# Revit family: RN 90024 Optifitt-Serra-Réduction
name_source: partatom
category: Rohrformteile
units: mm (PartAtom-declared; Revit-internal decimal feet)

## family parameters
Arbeitsebenenbasiert = Nein
Beim Laden mit Abzugskörper schneiden = Nein
Bemaßung runder Anschluss = Durchmesser verwenden
Gemeinsam genutzt = Nein
Immer vertikal = Ja
Teiletyp = Übergang

## types (26) — shared parameters
1.010.00.2 Blattnummer der Richtlinie = 29
1.010.00.3 Ausgabedatum (Monat) der Richtlinie = 201308
1.010.00.4 Herstellername = R. Nussbaum AG
1.010.00.5 Revisionsdatum der Datei = 20190521
1.010.00.6 Webadresse des Herstellers = http://www.nussbaum.ch
1.100.00.4 Produktbezeichnung = Versorgung
1.110.00.2 Index = 3
1.110.00.4 Produktbezeichnung = Optifitt-Serra
1.960/3L.00.8 Link (URL) = https://www.nussbaum.ch
29.700.00.4 Produktname = Optifitt-Serra-Reduktion
29.700.00.5 Produktkennung = 2
29.700.00.6 Querschnittsform = 1
29.700.00.7 Nennweitensystem = DN
29.700.00.8 Nenndrucksystem = PN
29.710.02.4 Nenndruck = 16
29.710.02.5 max. zul. Überdruck [hPa] = 1600
29.710.02.7 max. zul. Dauer-Betriebsdruck [hPa] = 1600
29.710.02.9 max. zul. Dauer-Betriebstemperatur [°C] = 90
Connector Visibility = Nein
EnclosingSpace Visibility = Nein
R. Nussbaum AG 90024.47 de Visibility = Nein

## per-type parameters (varying)
- DN=50x32: 1.800.00.3 TGA-Nummer=01900300000000000000000000000000000000000000000014000000000000000045; 1.800.00.4 Kommentarfeld=90024.40, Optifitt-Serra-Reduktion, DN=50x32, L=37, R=2, Rp=1¼; 1.810.00.3 Hersteller-Bestellnummer=90024.40; 1.810.00.4 DATANORM-Nummer=90024.40; 1.810.00.6 GTIN-Nummer=7612945033598; 29.710.02.10 Formstück-Gewicht [kg]=0.342; 29.710.02.3 Benennung=Optifitt-Serra-Reduktion, DN=50x32, L=37, R=2, Rp=1¼; CONNECTOR0_DIAMETER_dX_0r=32 mm; CONNECTOR0_dX_01=19 mm; CONNECTOR0_ref_dX=19 mm; CONNECTOR1_DIAMETER_dX_0r=50 mm; CONNECTOR1_dX_00=13 mm; CONNECTOR1_dX_01=37 mm; CONNECTOR1_ref_dX=37 mm; R. Nussbaum AG 90024.20 de Visibility=Nein; R. Nussbaum AG 90024.21 de Visibility=Nein; R. Nussbaum AG 90024.22 de Visibility=Nein; R. Nussbaum AG 90024.23 de Visibility=Nein; R. Nussbaum AG 90024.25 de Visibility=Nein; R. Nussbaum AG 90024.26 de Visibility=Nein; R. Nussbaum AG 90024.27 de Visibility=Nein; R. Nussbaum AG 90024.28 de Visibility=Nein; R. Nussbaum AG 90024.29 de Visibility=Nein; R. Nussbaum AG 90024.30 de Visibility=Nein; R. Nussbaum AG 90024.31 de Visibility=Nein; R. Nussbaum AG 90024.32 de Visibility=Nein; R. Nussbaum AG 90024.33 de Visibility=Nein; R. Nussbaum AG 90024.34 de Visibility=Nein; R. Nussbaum AG 90024.35 de Visibility=Nein; R. Nussbaum AG 90024.36 de Visibility=Nein; R. Nussbaum AG 90024.37 de Visibility=Nein; R. Nussbaum AG 90024.38 de Visibility=Nein; R. Nussbaum AG 90024.39 de Visibility=Nein; R. Nussbaum AG 90024.40 de Visibility=Ja; R. Nussbaum AG 90024.41 de Visibility=Nein; R. Nussbaum AG 90024.42 de Visibility=Nein; R. Nussbaum AG 90024.43 de Visibility=Nein; R. Nussbaum AG 90024.44 de Visibility=Nein; R. Nussbaum AG 90024.45 de Visibility=Nein; R. Nussbaum AG 90024.46 de Visibility=Nein
- DN=32x15: 1.800.00.3 TGA-Nummer=01900300000000000000000000000000000000000000000014000000000000000044; 1.800.00.4 Kommentarfeld=90024.30, Optifitt-Serra-Reduktion, DN=32x15, L=31, R=1¼, Rp=½; 1.810.00.3 Hersteller-Bestellnummer=90024.30; 1.810.00.4 DATANORM-Nummer=90024.30; 1.810.00.6 GTIN-Nummer=7612945033499; 29.710.02.10 Formstück-Gewicht [kg]=0.168; 29.710.02.3 Benennung=Optifitt-Serra-Reduktion, DN=32x15, L=31, R=1¼, Rp=½; CONNECTOR0_DIAMETER_dX_0r=15 mm; CONNECTOR0_dX_01=13 mm; CONNECTOR0_ref_dX=13 mm; CONNECTOR1_DIAMETER_dX_0r=32 mm; CONNECTOR1_dX_00=12 mm  [stored 0.0393701 ft]; CONNECTOR1_dX_01=31 mm; CONNECTOR1_ref_dX=31 mm; R. Nussbaum AG 90024.20 de Visibility=Nein; R. Nussbaum AG 90024.21 de Visibility=Nein; R. Nussbaum AG 90024.22 de Visibility=Nein; R. Nussbaum AG 90024.23 de Visibility=Nein; R. Nussbaum AG 90024.25 de Visibility=Nein; R. Nussbaum AG 90024.26 de Visibility=Nein; R. Nussbaum AG 90024.27 de Visibility=Nein; R. Nussbaum AG 90024.28 de Visibility=Nein; R. Nussbaum AG 90024.29 de Visibility=Nein; R. Nussbaum AG 90024.30 de Visibility=Ja; R. Nussbaum AG 90024.31 de Visibility=Nein; R. Nussbaum AG 90024.32 de Visibility=Nein; R. Nussbaum AG 90024.33 de Visibility=Nein; R. Nussbaum AG 90024.34 de Visibility=Nein; R. Nussbaum AG 90024.35 de Visibility=Nein; R. Nussbaum AG 90024.36 de Visibility=Nein; R. Nussbaum AG 90024.37 de Visibility=Nein; R. Nussbaum AG 90024.38 de Visibility=Nein; R. Nussbaum AG 90024.39 de Visibility=Nein; R. Nussbaum AG 90024.40 de Visibility=Nein; R. Nussbaum AG 90024.41 de Visibility=Nein; R. Nussbaum AG 90024.42 de Visibility=Nein; R. Nussbaum AG 90024.43 de Visibility=Nein; R. Nussbaum AG 90024.44 de Visibility=Nein; R. Nussbaum AG 90024.45 de Visibility=Nein; R. Nussbaum AG 90024.46 de Visibility=Nein
- DN=12x6: 1.800.00.3 TGA-Nummer=01900300000000000000000000000000000000000000000014000000000000000043; 1.800.00.4 Kommentarfeld=90024.20, Optifitt-Serra-Reduktion, DN=12x6, L=17, R=3/8, Rp=1/8; 1.810.00.3 Hersteller-Bestellnummer=90024.20; 1.810.00.4 DATANORM-Nummer=90024.20; 1.810.00.6 GTIN-Nummer=7612945723642; 29.710.02.10 Formstück-Gewicht [kg]=0.016; 29.710.02.3 Benennung=Optifitt-Serra-Reduktion, DN=12x6, L=17, R=3/8, Rp=1/8; CONNECTOR0_DIAMETER_dX_0r=6 mm  [stored 0.019685 ft]; CONNECTOR0_dX_01=7 mm  [stored 0.0229659 ft]; CONNECTOR0_ref_dX=7 mm  [stored 0.0229659 ft]; CONNECTOR1_DIAMETER_dX_0r=10 mm  [stored 0.0328084 ft]; CONNECTOR1_dX_00=7 mm  [stored 0.0229659 ft]; CONNECTOR1_dX_01=17 mm; CONNECTOR1_ref_dX=17 mm; R. Nussbaum AG 90024.20 de Visibility=Ja; R. Nussbaum AG 90024.21 de Visibility=Nein; R. Nussbaum AG 90024.22 de Visibility=Nein; R. Nussbaum AG 90024.23 de Visibility=Nein; R. Nussbaum AG 90024.25 de Visibility=Nein; R. Nussbaum AG 90024.26 de Visibility=Nein; R. Nussbaum AG 90024.27 de Visibility=Nein; R. Nussbaum AG 90024.28 de Visibility=Nein; R. Nussbaum AG 90024.29 de Visibility=Nein; R. Nussbaum AG 90024.30 de Visibility=Nein; R. Nussbaum AG 90024.31 de Visibility=Nein; R. Nussbaum AG 90024.32 de Visibility=Nein; R. Nussbaum AG 90024.33 de Visibility=Nein; R. Nussbaum AG 90024.34 de Visibility=Nein; R. Nussbaum AG 90024.35 de Visibility=Nein; R. Nussbaum AG 90024.36 de Visibility=Nein; R. Nussbaum AG 90024.37 de Visibility=Nein; R. Nussbaum AG 90024.38 de Visibility=Nein; R. Nussbaum AG 90024.39 de Visibility=Nein; R. Nussbaum AG 90024.40 de Visibility=Nein; R. Nussbaum AG 90024.41 de Visibility=Nein; R. Nussbaum AG 90024.42 de Visibility=Nein; R. Nussbaum AG 90024.43 de Visibility=Nein; R. Nussbaum AG 90024.44 de Visibility=Nein; R. Nussbaum AG 90024.45 de Visibility=Nein; R. Nussbaum AG 90024.46 de Visibility=Nein
- DN=80x65: 1.800.00.3 TGA-Nummer=01900300000000000000000000000000000000000000000014000000000000000023; 1.800.00.4 Kommentarfeld=90024.46, Optifitt-Serra-Reduktion, DN=80x65, L=47, R=3, Rp=2½; 1.810.00.3 Hersteller-Bestellnummer=90024.46; 1.810.00.4 DATANORM-Nummer=90024.46; 1.810.00.6 GTIN-Nummer=7612945723659; 29.710.02.10 Formstück-Gewicht [kg]=0.614; 29.710.02.3 Benennung=Optifitt-Serra-Reduktion, DN=80x65, L=47, R=3, Rp=2½; CONNECTOR0_DIAMETER_dX_0r=65 mm; CONNECTOR0_dX_01=27 mm; CONNECTOR0_ref_dX=27 mm; CONNECTOR1_DIAMETER_dX_0r=80 mm; CONNECTOR1_dX_00=17 mm; CONNECTOR1_dX_01=47 mm; CONNECTOR1_ref_dX=47 mm; Hersteller=R. Nussbaum AG; Modell=90024.46; R. Nussbaum AG 90024.20 de Visibility=Nein; R. Nussbaum AG 90024.21 de Visibility=Nein; R. Nussbaum AG 90024.22 de Visibility=Nein; R. Nussbaum AG 90024.23 de Visibility=Nein; R. Nussbaum AG 90024.25 de Visibility=Nein; R. Nussbaum AG 90024.26 de Visibility=Nein; R. Nussbaum AG 90024.27 de Visibility=Nein; R. Nussbaum AG 90024.28 de Visibility=Nein; R. Nussbaum AG 90024.29 de Visibility=Nein; R. Nussbaum AG 90024.30 de Visibility=Nein; R. Nussbaum AG 90024.31 de Visibility=Nein; R. Nussbaum AG 90024.32 de Visibility=Nein; R. Nussbaum AG 90024.33 de Visibility=Nein; R. Nussbaum AG 90024.34 de Visibility=Nein; R. Nussbaum AG 90024.35 de Visibility=Nein; R. Nussbaum AG 90024.36 de Visibility=Nein; R. Nussbaum AG 90024.37 de Visibility=Nein; R. Nussbaum AG 90024.38 de Visibility=Nein; R. Nussbaum AG 90024.39 de Visibility=Nein; R. Nussbaum AG 90024.40 de Visibility=Nein; R. Nussbaum AG 90024.41 de Visibility=Nein; R. Nussbaum AG 90024.42 de Visibility=Nein; R. Nussbaum AG 90024.43 de Visibility=Nein; R. Nussbaum AG 90024.44 de Visibility=Nein; R. Nussbaum AG 90024.45 de Visibility=Nein; R. Nussbaum AG 90024.46 de Visibility=Ja; Typenkommentare=Optifitt-Serra-Réduction DN=80x65; URL=https://www.nussbaum.ch
- DN=65x50: 1.800.00.3 TGA-Nummer=01900300000000000000000000000000000000000000000014000000000000000022; 1.800.00.4 Kommentarfeld=90024.45, Optifitt-Serra-Reduktion, DN=65x50, L=41, R=2½, Rp=2; 1.810.00.3 Hersteller-Bestellnummer=90024.45; 1.810.00.4 DATANORM-Nummer=90024.45; 1.810.00.5 StLB-Nummer=214.538; 1.810.00.6 GTIN-Nummer=7612945033642; 29.710.02.10 Formstück-Gewicht [kg]=0.495; 29.710.02.3 Benennung=Optifitt-Serra-Reduktion, DN=65x50, L=41, R=2½, Rp=2; CONNECTOR0_DIAMETER_dX_0r=50 mm; CONNECTOR0_dX_01=24 mm; CONNECTOR0_ref_dX=24 mm; CONNECTOR1_DIAMETER_dX_0r=65 mm; CONNECTOR1_dX_00=14 mm  [stored 0.0459318 ft]; CONNECTOR1_dX_01=41 mm; CONNECTOR1_ref_dX=41 mm; Hersteller=R. Nussbaum AG; Modell=90024.45; R. Nussbaum AG 90024.20 de Visibility=Nein; R. Nussbaum AG 90024.21 de Visibility=Nein; R. Nussbaum AG 90024.22 de Visibility=Nein; R. Nussbaum AG 90024.23 de Visibility=Nein; R. Nussbaum AG 90024.25 de Visibility=Nein; R. Nussbaum AG 90024.26 de Visibility=Nein; R. Nussbaum AG 90024.27 de Visibility=Nein; R. Nussbaum AG 90024.28 de Visibility=Nein; R. Nussbaum AG 90024.29 de Visibility=Nein; R. Nussbaum AG 90024.30 de Visibility=Nein; R. Nussbaum AG 90024.31 de Visibility=Nein; R. Nussbaum AG 90024.32 de Visibility=Nein; R. Nussbaum AG 90024.33 de Visibility=Nein; R. Nussbaum AG 90024.34 de Visibility=Nein; R. Nussbaum AG 90024.35 de Visibility=Nein; R. Nussbaum AG 90024.36 de Visibility=Nein; R. Nussbaum AG 90024.37 de Visibility=Nein; R. Nussbaum AG 90024.38 de Visibility=Nein; R. Nussbaum AG 90024.39 de Visibility=Nein; R. Nussbaum AG 90024.40 de Visibility=Nein; R. Nussbaum AG 90024.41 de Visibility=Nein; R. Nussbaum AG 90024.42 de Visibility=Nein; R. Nussbaum AG 90024.43 de Visibility=Nein; R. Nussbaum AG 90024.44 de Visibility=Nein; R. Nussbaum AG 90024.45 de Visibility=Ja; R. Nussbaum AG 90024.46 de Visibility=Nein; Typenkommentare=Optifitt-Serra-Réduction DN=65x50; URL=https://www.nussbaum.ch
- DN=65x40: 1.800.00.3 TGA-Nummer=01900300000000000000000000000000000000000000000014000000000000000021; 1.800.00.4 Kommentarfeld=90024.44, Optifitt-Serra-Reduktion, DN=65x40, L=41, R=2½, Rp=1½; 1.810.00.3 Hersteller-Bestellnummer=90024.44; 1.810.00.4 DATANORM-Nummer=90024.44; 1.810.00.6 GTIN-Nummer=7612945033635; 29.710.02.10 Formstück-Gewicht [kg]=0.609; 29.710.02.3 Benennung=Optifitt-Serra-Reduktion, DN=65x40, L=41, R=2½, Rp=1½; CONNECTOR0_DIAMETER_dX_0r=40 mm; CONNECTOR0_dX_01=19 mm; CONNECTOR0_ref_dX=19 mm; CONNECTOR1_DIAMETER_dX_0r=65 mm; CONNECTOR1_dX_00=14 mm  [stored 0.0459318 ft]; CONNECTOR1_dX_01=41 mm; CONNECTOR1_ref_dX=41 mm; Hersteller=R. Nussbaum AG; Modell=90024.44; R. Nussbaum AG 90024.20 de Visibility=Nein; R. Nussbaum AG 90024.21 de Visibility=Nein; R. Nussbaum AG 90024.22 de Visibility=Nein; R. Nussbaum AG 90024.23 de Visibility=Nein; R. Nussbaum AG 90024.25 de Visibility=Nein; R. Nussbaum AG 90024.26 de Visibility=Nein; R. Nussbaum AG 90024.27 de Visibility=Nein; R. Nussbaum AG 90024.28 de Visibility=Nein; R. Nussbaum AG 90024.29 de Visibility=Nein; R. Nussbaum AG 90024.30 de Visibility=Nein; R. Nussbaum AG 90024.31 de Visibility=Nein; R. Nussbaum AG 90024.32 de Visibility=Nein; R. Nussbaum AG 90024.33 de Visibility=Nein; R. Nussbaum AG 90024.34 de Visibility=Nein; R. Nussbaum AG 90024.35 de Visibility=Nein; R. Nussbaum AG 90024.36 de Visibility=Nein; R. Nussbaum AG 90024.37 de Visibility=Nein; R. Nussbaum AG 90024.38 de Visibility=Nein; R. Nussbaum AG 90024.39 de Visibility=Nein; R. Nussbaum AG 90024.40 de Visibility=Nein; R. Nussbaum AG 90024.41 de Visibility=Nein; R. Nussbaum AG 90024.42 de Visibility=Nein; R. Nussbaum AG 90024.43 de Visibility=Nein; R. Nussbaum AG 90024.44 de Visibility=Ja; R. Nussbaum AG 90024.45 de Visibility=Nein; R. Nussbaum AG 90024.46 de Visibility=Nein; Typenkommentare=Optifitt-Serra-Réduction DN=65x40; URL=https://www.nussbaum.ch
- DN=65x32: 1.800.00.3 TGA-Nummer=01900300000000000000000000000000000000000000000014000000000000000020; 1.800.00.4 Kommentarfeld=90024.43, Optifitt-Serra-Reduktion, DN=65x32, L=41, R=2½, Rp=1¼; 1.810.00.3 Hersteller-Bestellnummer=90024.43; 1.810.00.4 DATANORM-Nummer=90024.43; 1.810.00.6 GTIN-Nummer=7612945033628; 29.710.02.10 Formstück-Gewicht [kg]=0.662; 29.710.02.3 Benennung=Optifitt-Serra-Reduktion, DN=65x32, L=41, R=2½, Rp=1¼; CONNECTOR0_DIAMETER_dX_0r=32 mm; CONNECTOR0_dX_01=19 mm; CONNECTOR0_ref_dX=19 mm; CONNECTOR1_DIAMETER_dX_0r=65 mm; CONNECTOR1_dX_00=14 mm  [stored 0.0459318 ft]; CONNECTOR1_dX_01=41 mm; CONNECTOR1_ref_dX=41 mm; Hersteller=R. Nussbaum AG; Modell=90024.43; R. Nussbaum AG 90024.20 de Visibility=Nein; R. Nussbaum AG 90024.21 de Visibility=Nein; R. Nussbaum AG 90024.22 de Visibility=Nein; R. Nussbaum AG 90024.23 de Visibility=Nein; R. Nussbaum AG 90024.25 de Visibility=Nein; R. Nussbaum AG 90024.26 de Visibility=Nein; R. Nussbaum AG 90024.27 de Visibility=Nein; R. Nussbaum AG 90024.28 de Visibility=Nein; R. Nussbaum AG 90024.29 de Visibility=Nein; R. Nussbaum AG 90024.30 de Visibility=Nein; R. Nussbaum AG 90024.31 de Visibility=Nein; R. Nussbaum AG 90024.32 de Visibility=Nein; R. Nussbaum AG 90024.33 de Visibility=Nein; R. Nussbaum AG 90024.34 de Visibility=Nein; R. Nussbaum AG 90024.35 de Visibility=Nein; R. Nussbaum AG 90024.36 de Visibility=Nein; R. Nussbaum AG 90024.37 de Visibility=Nein; R. Nussbaum AG 90024.38 de Visibility=Nein; R. Nussbaum AG 90024.39 de Visibility=Nein; R. Nussbaum AG 90024.40 de Visibility=Nein; R. Nussbaum AG 90024.41 de Visibility=Nein; R. Nussbaum AG 90024.42 de Visibility=Nein; R. Nussbaum AG 90024.43 de Visibility=Ja; R. Nussbaum AG 90024.44 de Visibility=Nein; R. Nussbaum AG 90024.45 de Visibility=Nein; R. Nussbaum AG 90024.46 de Visibility=Nein; Typenkommentare=Optifitt-Serra-Réduction DN=65x32; URL=https://www.nussbaum.ch
- DN=65x25: 1.800.00.3 TGA-Nummer=01900300000000000000000000000000000000000000000014000000000000000019; 1.800.00.4 Kommentarfeld=90024.42, Optifitt-Serra-Reduktion, DN=65x25, L=41, R=2½, Rp=1; 1.810.00.3 Hersteller-Bestellnummer=90024.42; 1.810.00.4 DATANORM-Nummer=90024.42; 1.810.00.6 GTIN-Nummer=7612945033611; 29.710.02.10 Formstück-Gewicht [kg]=0.679; 29.710.02.3 Benennung=Optifitt-Serra-Reduktion, DN=65x25, L=41, R=2½, Rp=1; CONNECTOR0_DIAMETER_dX_0r=25 mm  [stored 0.082021 ft]; CONNECTOR0_dX_01=17 mm; CONNECTOR0_ref_dX=17 mm; CONNECTOR1_DIAMETER_dX_0r=65 mm; CONNECTOR1_dX_00=14 mm  [stored 0.0459318 ft]; CONNECTOR1_dX_01=41 mm; CONNECTOR1_ref_dX=41 mm; Hersteller=R. Nussbaum AG; Modell=90024.42; R. Nussbaum AG 90024.20 de Visibility=Nein; R. Nussbaum AG 90024.21 de Visibility=Nein; R. Nussbaum AG 90024.22 de Visibility=Nein; R. Nussbaum AG 90024.23 de Visibility=Nein; R. Nussbaum AG 90024.25 de Visibility=Nein; R. Nussbaum AG 90024.26 de Visibility=Nein; R. Nussbaum AG 90024.27 de Visibility=Nein; R. Nussbaum AG 90024.28 de Visibility=Nein; R. Nussbaum AG 90024.29 de Visibility=Nein; R. Nussbaum AG 90024.30 de Visibility=Nein; R. Nussbaum AG 90024.31 de Visibility=Nein; R. Nussbaum AG 90024.32 de Visibility=Nein; R. Nussbaum AG 90024.33 de Visibility=Nein; R. Nussbaum AG 90024.34 de Visibility=Nein; R. Nussbaum AG 90024.35 de Visibility=Nein; R. Nussbaum AG 90024.36 de Visibility=Nein; R. Nussbaum AG 90024.37 de Visibility=Nein; R. Nussbaum AG 90024.38 de Visibility=Nein; R. Nussbaum AG 90024.39 de Visibility=Nein; R. Nussbaum AG 90024.40 de Visibility=Nein; R. Nussbaum AG 90024.41 de Visibility=Nein; R. Nussbaum AG 90024.42 de Visibility=Ja; R. Nussbaum AG 90024.43 de Visibility=Nein; R. Nussbaum AG 90024.44 de Visibility=Nein; R. Nussbaum AG 90024.45 de Visibility=Nein; R. Nussbaum AG 90024.46 de Visibility=Nein; Typenkommentare=Optifitt-Serra-Réduction DN=65x25; URL=https://www.nussbaum.ch
- DN=50x40: 1.800.00.3 TGA-Nummer=01900300000000000000000000000000000000000000000014000000000000000018; 1.800.00.4 Kommentarfeld=90024.41, Optifitt-Serra-Reduktion, DN=50x40, L=37, R=2, Rp=1½; 1.810.00.3 Hersteller-Bestellnummer=90024.41; 1.810.00.4 DATANORM-Nummer=90024.41; 1.810.00.5 StLB-Nummer=214.537; 1.810.00.6 GTIN-Nummer=7612945033604; 29.710.02.10 Formstück-Gewicht [kg]=0.287; 29.710.02.3 Benennung=Optifitt-Serra-Reduktion, DN=50x40, L=37, R=2, Rp=1½; CONNECTOR0_DIAMETER_dX_0r=40 mm; CONNECTOR0_dX_01=19 mm; CONNECTOR0_ref_dX=19 mm; CONNECTOR1_DIAMETER_dX_0r=50 mm; CONNECTOR1_dX_00=13 mm; CONNECTOR1_dX_01=37 mm; CONNECTOR1_ref_dX=37 mm; Hersteller=R. Nussbaum AG; Modell=90024.41; R. Nussbaum AG 90024.20 de Visibility=Nein; R. Nussbaum AG 90024.21 de Visibility=Nein; R. Nussbaum AG 90024.22 de Visibility=Nein; R. Nussbaum AG 90024.23 de Visibility=Nein; R. Nussbaum AG 90024.25 de Visibility=Nein; R. Nussbaum AG 90024.26 de Visibility=Nein; R. Nussbaum AG 90024.27 de Visibility=Nein; R. Nussbaum AG 90024.28 de Visibility=Nein; R. Nussbaum AG 90024.29 de Visibility=Nein; R. Nussbaum AG 90024.30 de Visibility=Nein; R. Nussbaum AG 90024.31 de Visibility=Nein; R. Nussbaum AG 90024.32 de Visibility=Nein; R. Nussbaum AG 90024.33 de Visibility=Nein; R. Nussbaum AG 90024.34 de Visibility=Nein; R. Nussbaum AG 90024.35 de Visibility=Nein; R. Nussbaum AG 90024.36 de Visibility=Nein; R. Nussbaum AG 90024.37 de Visibility=Nein; R. Nussbaum AG 90024.38 de Visibility=Nein; R. Nussbaum AG 90024.39 de Visibility=Nein; R. Nussbaum AG 90024.40 de Visibility=Nein; R. Nussbaum AG 90024.41 de Visibility=Ja; R. Nussbaum AG 90024.42 de Visibility=Nein; R. Nussbaum AG 90024.43 de Visibility=Nein; R. Nussbaum AG 90024.44 de Visibility=Nein; R. Nussbaum AG 90024.45 de Visibility=Nein; R. Nussbaum AG 90024.46 de Visibility=Nein; Typenkommentare=Optifitt-Serra-Réduction DN=50x40; URL=https://www.nussbaum.ch
- DN=50x25: 1.800.00.3 TGA-Nummer=01900300000000000000000000000000000000000000000014000000000000000017; 1.800.00.4 Kommentarfeld=90024.39, Optifitt-Serra-Reduktion, DN=50x25, L=37, R=2, Rp=1; 1.810.00.3 Hersteller-Bestellnummer=90024.39; 1.810.00.4 DATANORM-Nummer=90024.39; 1.810.00.6 GTIN-Nummer=7612945033581; 29.710.02.10 Formstück-Gewicht [kg]=0.395; 29.710.02.3 Benennung=Optifitt-Serra-Reduktion, DN=50x25, L=37, R=2, Rp=1; CONNECTOR0_DIAMETER_dX_0r=25 mm  [stored 0.082021 ft]; CONNECTOR0_dX_01=17 mm; CONNECTOR0_ref_dX=17 mm; CONNECTOR1_DIAMETER_dX_0r=50 mm; CONNECTOR1_dX_00=13 mm; CONNECTOR1_dX_01=37 mm; CONNECTOR1_ref_dX=37 mm; Hersteller=R. Nussbaum AG; Modell=90024.39; R. Nussbaum AG 90024.20 de Visibility=Nein; R. Nussbaum AG 90024.21 de Visibility=Nein; R. Nussbaum AG 90024.22 de Visibility=Nein; R. Nussbaum AG 90024.23 de Visibility=Nein; R. Nussbaum AG 90024.25 de Visibility=Nein; R. Nussbaum AG 90024.26 de Visibility=Nein; R. Nussbaum AG 90024.27 de Visibility=Nein; R. Nussbaum AG 90024.28 de Visibility=Nein; R. Nussbaum AG 90024.29 de Visibility=Nein; R. Nussbaum AG 90024.30 de Visibility=Nein; R. Nussbaum AG 90024.31 de Visibility=Nein; R. Nussbaum AG 90024.32 de Visibility=Nein; R. Nussbaum AG 90024.33 de Visibility=Nein; R. Nussbaum AG 90024.34 de Visibility=Nein; R. Nussbaum AG 90024.35 de Visibility=Nein; R. Nussbaum AG 90024.36 de Visibility=Nein; R. Nussbaum AG 90024.37 de Visibility=Nein; R. Nussbaum AG 90024.38 de Visibility=Nein; R. Nussbaum AG 90024.39 de Visibility=Ja; R. Nussbaum AG 90024.40 de Visibility=Nein; R. Nussbaum AG 90024.41 de Visibility=Nein; R. Nussbaum AG 90024.42 de Visibility=Nein; R. Nussbaum AG 90024.43 de Visibility=Nein; R. Nussbaum AG 90024.44 de Visibility=Nein; R. Nussbaum AG 90024.45 de Visibility=Nein; R. Nussbaum AG 90024.46 de Visibility=Nein; Typenkommentare=Optifitt-Serra-Réduction DN=50x25; URL=https://www.nussbaum.ch
- DN=50x20: 1.800.00.3 TGA-Nummer=01900300000000000000000000000000000000000000000014000000000000000016; 1.800.00.4 Kommentarfeld=90024.38, Optifitt-Serra-Reduktion, DN=50x20, L=37, R=2, Rp=¾; 1.810.00.3 Hersteller-Bestellnummer=90024.38; 1.810.00.4 DATANORM-Nummer=90024.38; 1.810.00.6 GTIN-Nummer=7612945033574; 29.710.02.10 Formstück-Gewicht [kg]=0.396; 29.710.02.3 Benennung=Optifitt-Serra-Reduktion, DN=50x20, L=37, R=2, Rp=¾; CONNECTOR0_DIAMETER_dX_0r=20 mm; CONNECTOR0_dX_01=15 mm; CONNECTOR0_ref_dX=15 mm; CONNECTOR1_DIAMETER_dX_0r=50 mm; CONNECTOR1_dX_00=13 mm; CONNECTOR1_dX_01=37 mm; CONNECTOR1_ref_dX=37 mm; Hersteller=R. Nussbaum AG; Modell=90024.38; R. Nussbaum AG 90024.20 de Visibility=Nein; R. Nussbaum AG 90024.21 de Visibility=Nein; R. Nussbaum AG 90024.22 de Visibility=Nein; R. Nussbaum AG 90024.23 de Visibility=Nein; R. Nussbaum AG 90024.25 de Visibility=Nein; R. Nussbaum AG 90024.26 de Visibility=Nein; R. Nussbaum AG 90024.27 de Visibility=Nein; R. Nussbaum AG 90024.28 de Visibility=Nein; R. Nussbaum AG 90024.29 de Visibility=Nein; R. Nussbaum AG 90024.30 de Visibility=Nein; R. Nussbaum AG 90024.31 de Visibility=Nein; R. Nussbaum AG 90024.32 de Visibility=Nein; R. Nussbaum AG 90024.33 de Visibility=Nein; R. Nussbaum AG 90024.34 de Visibility=Nein; R. Nussbaum AG 90024.35 de Visibility=Nein; R. Nussbaum AG 90024.36 de Visibility=Nein; R. Nussbaum AG 90024.37 de Visibility=Nein; R. Nussbaum AG 90024.38 de Visibility=Ja; R. Nussbaum AG 90024.39 de Visibility=Nein; R. Nussbaum AG 90024.40 de Visibility=Nein; R. Nussbaum AG 90024.41 de Visibility=Nein; R. Nussbaum AG 90024.42 de Visibility=Nein; R. Nussbaum AG 90024.43 de Visibility=Nein; R. Nussbaum AG 90024.44 de Visibility=Nein; R. Nussbaum AG 90024.45 de Visibility=Nein; R. Nussbaum AG 90024.46 de Visibility=Nein; Typenkommentare=Optifitt-Serra-Réduction DN=50x20; URL=https://www.nussbaum.ch
- DN=50x15: 1.800.00.3 TGA-Nummer=01900300000000000000000000000000000000000000000014000000000000000015; 1.800.00.4 Kommentarfeld=90024.37, Optifitt-Serra-Reduktion, DN=50x15, L=37, R=2, Rp=½; 1.810.00.3 Hersteller-Bestellnummer=90024.37; 1.810.00.4 DATANORM-Nummer=90024.37; 1.810.00.6 GTIN-Nummer=7612945033567; 29.710.02.10 Formstück-Gewicht [kg]=0.399; 29.710.02.3 Benennung=Optifitt-Serra-Reduktion, DN=50x15, L=37, R=2, Rp=½; CONNECTOR0_DIAMETER_dX_0r=15 mm; CONNECTOR0_dX_01=13 mm; CONNECTOR0_ref_dX=13 mm; CONNECTOR1_DIAMETER_dX_0r=50 mm; CONNECTOR1_dX_00=13 mm; CONNECTOR1_dX_01=37 mm; CONNECTOR1_ref_dX=37 mm; R. Nussbaum AG 90024.20 de Visibility=Nein; R. Nussbaum AG 90024.21 de Visibility=Nein; R. Nussbaum AG 90024.22 de Visibility=Nein; R. Nussbaum AG 90024.23 de Visibility=Nein; R. Nussbaum AG 90024.25 de Visibility=Nein; R. Nussbaum AG 90024.26 de Visibility=Nein; R. Nussbaum AG 90024.27 de Visibility=Nein; R. Nussbaum AG 90024.28 de Visibility=Nein; R. Nussbaum AG 90024.29 de Visibility=Nein; R. Nussbaum AG 90024.30 de Visibility=Nein; R. Nussbaum AG 90024.31 de Visibility=Nein; R. Nussbaum AG 90024.32 de Visibility=Nein; R. Nussbaum AG 90024.33 de Visibility=Nein; R. Nussbaum AG 90024.34 de Visibility=Nein; R. Nussbaum AG 90024.35 de Visibility=Nein; R. Nussbaum AG 90024.36 de Visibility=Nein; R. Nussbaum AG 90024.37 de Visibility=Ja; R. Nussbaum AG 90024.38 de Visibility=Nein; R. Nussbaum AG 90024.39 de Visibility=Nein; R. Nussbaum AG 90024.40 de Visibility=Nein; R. Nussbaum AG 90024.41 de Visibility=Nein; R. Nussbaum AG 90024.42 de Visibility=Nein; R. Nussbaum AG 90024.43 de Visibility=Nein; R. Nussbaum AG 90024.44 de Visibility=Nein; R. Nussbaum AG 90024.45 de Visibility=Nein; R. Nussbaum AG 90024.46 de Visibility=Nein
- DN=40x32: 1.800.00.3 TGA-Nummer=01900300000000000000000000000000000000000000000014000000000000000014; 1.800.00.4 Kommentarfeld=90024.36, Optifitt-Serra-Reduktion, DN=40x32, L=31, R=1½, Rp=1¼; 1.810.00.3 Hersteller-Bestellnummer=90024.36; 1.810.00.4 DATANORM-Nummer=90024.36; 1.810.00.5 StLB-Nummer=214.536; 1.810.00.6 GTIN-Nummer=7612945033550; 29.710.02.10 Formstück-Gewicht [kg]=0.136; 29.710.02.3 Benennung=Optifitt-Serra-Reduktion, DN=40x32, L=31, R=1½, Rp=1¼; CONNECTOR0_DIAMETER_dX_0r=32 mm; CONNECTOR0_dX_01=19 mm; CONNECTOR0_ref_dX=19 mm; CONNECTOR1_DIAMETER_dX_0r=40 mm; CONNECTOR1_dX_00=12 mm  [stored 0.0393701 ft]; CONNECTOR1_dX_01=31 mm; CONNECTOR1_ref_dX=31 mm; R. Nussbaum AG 90024.20 de Visibility=Nein; R. Nussbaum AG 90024.21 de Visibility=Nein; R. Nussbaum AG 90024.22 de Visibility=Nein; R. Nussbaum AG 90024.23 de Visibility=Nein; R. Nussbaum AG 90024.25 de Visibility=Nein; R. Nussbaum AG 90024.26 de Visibility=Nein; R. Nussbaum AG 90024.27 de Visibility=Nein; R. Nussbaum AG 90024.28 de Visibility=Nein; R. Nussbaum AG 90024.29 de Visibility=Nein; R. Nussbaum AG 90024.30 de Visibility=Nein; R. Nussbaum AG 90024.31 de Visibility=Nein; R. Nussbaum AG 90024.32 de Visibility=Nein; R. Nussbaum AG 90024.33 de Visibility=Nein; R. Nussbaum AG 90024.34 de Visibility=Nein; R. Nussbaum AG 90024.35 de Visibility=Nein; R. Nussbaum AG 90024.36 de Visibility=Ja; R. Nussbaum AG 90024.37 de Visibility=Nein; R. Nussbaum AG 90024.38 de Visibility=Nein; R. Nussbaum AG 90024.39 de Visibility=Nein; R. Nussbaum AG 90024.40 de Visibility=Nein; R. Nussbaum AG 90024.41 de Visibility=Nein; R. Nussbaum AG 90024.42 de Visibility=Nein; R. Nussbaum AG 90024.43 de Visibility=Nein; R. Nussbaum AG 90024.44 de Visibility=Nein; R. Nussbaum AG 90024.45 de Visibility=Nein; R. Nussbaum AG 90024.46 de Visibility=Nein
- DN=40x25: 1.800.00.3 TGA-Nummer=01900300000000000000000000000000000000000000000014000000000000000013; 1.800.00.4 Kommentarfeld=90024.35, Optifitt-Serra-Reduktion, DN=40x25, L=31, R=1½, Rp=1; 1.810.00.3 Hersteller-Bestellnummer=90024.35; 1.810.00.4 DATANORM-Nummer=90024.35; 1.810.00.6 GTIN-Nummer=7612945033543; 29.710.02.10 Formstück-Gewicht [kg]=0.197; 29.710.02.3 Benennung=Optifitt-Serra-Reduktion, DN=40x25, L=31, R=1½, Rp=1; CONNECTOR0_DIAMETER_dX_0r=25 mm  [stored 0.082021 ft]; CONNECTOR0_dX_01=17 mm; CONNECTOR0_ref_dX=17 mm; CONNECTOR1_DIAMETER_dX_0r=40 mm; CONNECTOR1_dX_00=12 mm  [stored 0.0393701 ft]; CONNECTOR1_dX_01=31 mm; CONNECTOR1_ref_dX=31 mm; R. Nussbaum AG 90024.20 de Visibility=Nein; R. Nussbaum AG 90024.21 de Visibility=Nein; R. Nussbaum AG 90024.22 de Visibility=Nein; R. Nussbaum AG 90024.23 de Visibility=Nein; R. Nussbaum AG 90024.25 de Visibility=Nein; R. Nussbaum AG 90024.26 de Visibility=Nein; R. Nussbaum AG 90024.27 de Visibility=Nein; R. Nussbaum AG 90024.28 de Visibility=Nein; R. Nussbaum AG 90024.29 de Visibility=Nein; R. Nussbaum AG 90024.30 de Visibility=Nein; R. Nussbaum AG 90024.31 de Visibility=Nein; R. Nussbaum AG 90024.32 de Visibility=Nein; R. Nussbaum AG 90024.33 de Visibility=Nein; R. Nussbaum AG 90024.34 de Visibility=Nein; R. Nussbaum AG 90024.35 de Visibility=Ja; R. Nussbaum AG 90024.36 de Visibility=Nein; R. Nussbaum AG 90024.37 de Visibility=Nein; R. Nussbaum AG 90024.38 de Visibility=Nein; R. Nussbaum AG 90024.39 de Visibility=Nein; R. Nussbaum AG 90024.40 de Visibility=Nein; R. Nussbaum AG 90024.41 de Visibility=Nein; R. Nussbaum AG 90024.42 de Visibility=Nein; R. Nussbaum AG 90024.43 de Visibility=Nein; R. Nussbaum AG 90024.44 de Visibility=Nein; R. Nussbaum AG 90024.45 de Visibility=Nein; R. Nussbaum AG 90024.46 de Visibility=Nein
- DN=40x20: 1.800.00.3 TGA-Nummer=01900300000000000000000000000000000000000000000014000000000000000012; 1.800.00.4 Kommentarfeld=90024.34, Optifitt-Serra-Reduktion, DN=40x20, L=31, R=1½, Rp=¾; 1.810.00.3 Hersteller-Bestellnummer=90024.34; 1.810.00.4 DATANORM-Nummer=90024.34; 1.810.00.6 GTIN-Nummer=7612945033536; 29.710.02.10 Formstück-Gewicht [kg]=0.222; 29.710.02.3 Benennung=Optifitt-Serra-Reduktion, DN=40x20, L=31, R=1½, Rp=¾; CONNECTOR0_DIAMETER_dX_0r=20 mm; CONNECTOR0_dX_01=15 mm; CONNECTOR0_ref_dX=15 mm; CONNECTOR1_DIAMETER_dX_0r=40 mm; CONNECTOR1_dX_00=12 mm  [stored 0.0393701 ft]; CONNECTOR1_dX_01=31 mm; CONNECTOR1_ref_dX=31 mm; Hersteller=R. Nussbaum AG; Modell=90024.34; R. Nussbaum AG 90024.20 de Visibility=Nein; R. Nussbaum AG 90024.21 de Visibility=Nein; R. Nussbaum AG 90024.22 de Visibility=Nein; R. Nussbaum AG 90024.23 de Visibility=Nein; R. Nussbaum AG 90024.25 de Visibility=Nein; R. Nussbaum AG 90024.26 de Visibility=Nein; R. Nussbaum AG 90024.27 de Visibility=Nein; R. Nussbaum AG 90024.28 de Visibility=Nein; R. Nussbaum AG 90024.29 de Visibility=Nein; R. Nussbaum AG 90024.30 de Visibility=Nein; R. Nussbaum AG 90024.31 de Visibility=Nein; R. Nussbaum AG 90024.32 de Visibility=Nein; R. Nussbaum AG 90024.33 de Visibility=Nein; R. Nussbaum AG 90024.34 de Visibility=Ja; R. Nussbaum AG 90024.35 de Visibility=Nein; R. Nussbaum AG 90024.36 de Visibility=Nein; R. Nussbaum AG 90024.37 de Visibility=Nein; R. Nussbaum AG 90024.38 de Visibility=Nein; R. Nussbaum AG 90024.39 de Visibility=Nein; R. Nussbaum AG 90024.40 de Visibility=Nein; R. Nussbaum AG 90024.41 de Visibility=Nein; R. Nussbaum AG 90024.42 de Visibility=Nein; R. Nussbaum AG 90024.43 de Visibility=Nein; R. Nussbaum AG 90024.44 de Visibility=Nein; R. Nussbaum AG 90024.45 de Visibility=Nein; R. Nussbaum AG 90024.46 de Visibility=Nein; Typenkommentare=Optifitt-Serra-Réduction DN=40x20; URL=https://www.nussbaum.ch
- DN=40x15: 1.800.00.3 TGA-Nummer=01900300000000000000000000000000000000000000000014000000000000000011; 1.800.00.4 Kommentarfeld=90024.33, Optifitt-Serra-Reduktion, DN=40x15, L=32, R=1½, Rp=½; 1.810.00.3 Hersteller-Bestellnummer=90024.33; 1.810.00.4 DATANORM-Nummer=90024.33; 1.810.00.6 GTIN-Nummer=7612945033529; 29.710.02.10 Formstück-Gewicht [kg]=0.228; 29.710.02.3 Benennung=Optifitt-Serra-Reduktion, DN=40x15, L=32, R=1½, Rp=½; CONNECTOR0_DIAMETER_dX_0r=15 mm; CONNECTOR0_dX_01=13 mm; CONNECTOR0_ref_dX=13 mm; CONNECTOR1_DIAMETER_dX_0r=40 mm; CONNECTOR1_dX_00=13 mm; CONNECTOR1_dX_01=32 mm; CONNECTOR1_ref_dX=32 mm; R. Nussbaum AG 90024.20 de Visibility=Nein; R. Nussbaum AG 90024.21 de Visibility=Nein; R. Nussbaum AG 90024.22 de Visibility=Nein; R. Nussbaum AG 90024.23 de Visibility=Nein; R. Nussbaum AG 90024.25 de Visibility=Nein; R. Nussbaum AG 90024.26 de Visibility=Nein; R. Nussbaum AG 90024.27 de Visibility=Nein; R. Nussbaum AG 90024.28 de Visibility=Nein; R. Nussbaum AG 90024.29 de Visibility=Nein; R. Nussbaum AG 90024.30 de Visibility=Nein; R. Nussbaum AG 90024.31 de Visibility=Nein; R. Nussbaum AG 90024.32 de Visibility=Nein; R. Nussbaum AG 90024.33 de Visibility=Ja; R. Nussbaum AG 90024.34 de Visibility=Nein; R. Nussbaum AG 90024.35 de Visibility=Nein; R. Nussbaum AG 90024.36 de Visibility=Nein; R. Nussbaum AG 90024.37 de Visibility=Nein; R. Nussbaum AG 90024.38 de Visibility=Nein; R. Nussbaum AG 90024.39 de Visibility=Nein; R. Nussbaum AG 90024.40 de Visibility=Nein; R. Nussbaum AG 90024.41 de Visibility=Nein; R. Nussbaum AG 90024.42 de Visibility=Nein; R. Nussbaum AG 90024.43 de Visibility=Nein; R. Nussbaum AG 90024.44 de Visibility=Nein; R. Nussbaum AG 90024.45 de Visibility=Nein; R. Nussbaum AG 90024.46 de Visibility=Nein
- DN=32x25: 1.800.00.3 TGA-Nummer=01900300000000000000000000000000000000000000000014000000000000000010; 1.800.00.4 Kommentarfeld=90024.32, Optifitt-Serra-Reduktion, DN=32x25, L=31, R=1¼, Rp=1; 1.810.00.3 Hersteller-Bestellnummer=90024.32; 1.810.00.4 DATANORM-Nummer=90024.32; 1.810.00.5 StLB-Nummer=214.535; 1.810.00.6 GTIN-Nummer=7612945033512; 29.710.02.10 Formstück-Gewicht [kg]=0.151; 29.710.02.3 Benennung=Optifitt-Serra-Reduktion, DN=32x25, L=31, R=1¼, Rp=1; CONNECTOR0_DIAMETER_dX_0r=25 mm  [stored 0.082021 ft]; CONNECTOR0_dX_01=17 mm; CONNECTOR0_ref_dX=17 mm; CONNECTOR1_DIAMETER_dX_0r=32 mm; CONNECTOR1_dX_00=12 mm  [stored 0.0393701 ft]; CONNECTOR1_dX_01=31 mm; CONNECTOR1_ref_dX=31 mm; R. Nussbaum AG 90024.20 de Visibility=Nein; R. Nussbaum AG 90024.21 de Visibility=Nein; R. Nussbaum AG 90024.22 de Visibility=Nein; R. Nussbaum AG 90024.23 de Visibility=Nein; R. Nussbaum AG 90024.25 de Visibility=Nein; R. Nussbaum AG 90024.26 de Visibility=Nein; R. Nussbaum AG 90024.27 de Visibility=Nein; R. Nussbaum AG 90024.28 de Visibility=Nein; R. Nussbaum AG 90024.29 de Visibility=Nein; R. Nussbaum AG 90024.30 de Visibility=Nein; R. Nussbaum AG 90024.31 de Visibility=Nein; R. Nussbaum AG 90024.32 de Visibility=Ja; R. Nussbaum AG 90024.33 de Visibility=Nein; R. Nussbaum AG 90024.34 de Visibility=Nein; R. Nussbaum AG 90024.35 de Visibility=Nein; R. Nussbaum AG 90024.36 de Visibility=Nein; R. Nussbaum AG 90024.37 de Visibility=Nein; R. Nussbaum AG 90024.38 de Visibility=Nein; R. Nussbaum AG 90024.39 de Visibility=Nein; R. Nussbaum AG 90024.40 de Visibility=Nein; R. Nussbaum AG 90024.41 de Visibility=Nein; R. Nussbaum AG 90024.42 de Visibility=Nein; R. Nussbaum AG 90024.43 de Visibility=Nein; R. Nussbaum AG 90024.44 de Visibility=Nein; R. Nussbaum AG 90024.45 de Visibility=Nein; R. Nussbaum AG 90024.46 de Visibility=Nein
- DN=32x20: 1.800.00.3 TGA-Nummer=01900300000000000000000000000000000000000000000014000000000000000009; 1.800.00.4 Kommentarfeld=90024.31, Optifitt-Serra-Reduktion, DN=32x20, L=31, R=1¼, Rp=¾; 1.810.00.3 Hersteller-Bestellnummer=90024.31; 1.810.00.4 DATANORM-Nummer=90024.31; 1.810.00.6 GTIN-Nummer=7612945033505; 29.710.02.10 Formstück-Gewicht [kg]=0.164; 29.710.02.3 Benennung=Optifitt-Serra-Reduktion, DN=32x20, L=31, R=1¼, Rp=¾; CONNECTOR0_DIAMETER_dX_0r=20 mm; CONNECTOR0_dX_01=15 mm; CONNECTOR0_ref_dX=15 mm; CONNECTOR1_DIAMETER_dX_0r=32 mm; CONNECTOR1_dX_00=12 mm  [stored 0.0393701 ft]; CONNECTOR1_dX_01=31 mm; CONNECTOR1_ref_dX=31 mm; Hersteller=R. Nussbaum AG; Modell=90024.31; R. Nussbaum AG 90024.20 de Visibility=Nein; R. Nussbaum AG 90024.21 de Visibility=Nein; R. Nussbaum AG 90024.22 de Visibility=Nein; R. Nussbaum AG 90024.23 de Visibility=Nein; R. Nussbaum AG 90024.25 de Visibility=Nein; R. Nussbaum AG 90024.26 de Visibility=Nein; R. Nussbaum AG 90024.27 de Visibility=Nein; R. Nussbaum AG 90024.28 de Visibility=Nein; R. Nussbaum AG 90024.29 de Visibility=Nein; R. Nussbaum AG 90024.30 de Visibility=Nein; R. Nussbaum AG 90024.31 de Visibility=Ja; R. Nussbaum AG 90024.32 de Visibility=Nein; R. Nussbaum AG 90024.33 de Visibility=Nein; R. Nussbaum AG 90024.34 de Visibility=Nein; R. Nussbaum AG 90024.35 de Visibility=Nein; R. Nussbaum AG 90024.36 de Visibility=Nein; R. Nussbaum AG 90024.37 de Visibility=Nein; R. Nussbaum AG 90024.38 de Visibility=Nein; R. Nussbaum AG 90024.39 de Visibility=Nein; R. Nussbaum AG 90024.40 de Visibility=Nein; R. Nussbaum AG 90024.41 de Visibility=Nein; R. Nussbaum AG 90024.42 de Visibility=Nein; R. Nussbaum AG 90024.43 de Visibility=Nein; R. Nussbaum AG 90024.44 de Visibility=Nein; R. Nussbaum AG 90024.45 de Visibility=Nein; R. Nussbaum AG 90024.46 de Visibility=Nein; Typenkommentare=Optifitt-Serra-Réduction DN=32x20; URL=https://www.nussbaum.ch
- DN=25x20: 1.800.00.3 TGA-Nummer=01900300000000000000000000000000000000000000000014000000000000000008; 1.800.00.4 Kommentarfeld=90024.29, Optifitt-Serra-Reduktion, DN=25x20, L=28, R=1, Rp=¾; 1.810.00.3 Hersteller-Bestellnummer=90024.29; 1.810.00.4 DATANORM-Nummer=90024.29; 1.810.00.5 StLB-Nummer=214.534; 1.810.00.6 GTIN-Nummer=7612945033482; 29.710.02.10 Formstück-Gewicht [kg]=0.078; 29.710.02.3 Benennung=Optifitt-Serra-Reduktion, DN=25x20, L=28, R=1, Rp=¾; CONNECTOR0_DIAMETER_dX_0r=20 mm; CONNECTOR0_dX_01=15 mm; CONNECTOR0_ref_dX=15 mm; CONNECTOR1_DIAMETER_dX_0r=25 mm  [stored 0.082021 ft]; CONNECTOR1_dX_00=11 mm; CONNECTOR1_dX_01=28 mm; CONNECTOR1_ref_dX=28 mm; Hersteller=R. Nussbaum AG; Modell=90024.29; R. Nussbaum AG 90024.20 de Visibility=Nein; R. Nussbaum AG 90024.21 de Visibility=Nein; R. Nussbaum AG 90024.22 de Visibility=Nein; R. Nussbaum AG 90024.23 de Visibility=Nein; R. Nussbaum AG 90024.25 de Visibility=Nein; R. Nussbaum AG 90024.26 de Visibility=Nein; R. Nussbaum AG 90024.27 de Visibility=Nein; R. Nussbaum AG 90024.28 de Visibility=Nein; R. Nussbaum AG 90024.29 de Visibility=Ja; R. Nussbaum AG 90024.30 de Visibility=Nein; R. Nussbaum AG 90024.31 de Visibility=Nein; R. Nussbaum AG 90024.32 de Visibility=Nein; R. Nussbaum AG 90024.33 de Visibility=Nein; R. Nussbaum AG 90024.34 de Visibility=Nein; R. Nussbaum AG 90024.35 de Visibility=Nein; R. Nussbaum AG 90024.36 de Visibility=Nein; R. Nussbaum AG 90024.37 de Visibility=Nein; R. Nussbaum AG 90024.38 de Visibility=Nein; R. Nussbaum AG 90024.39 de Visibility=Nein; R. Nussbaum AG 90024.40 de Visibility=Nein; R. Nussbaum AG 90024.41 de Visibility=Nein; R. Nussbaum AG 90024.42 de Visibility=Nein; R. Nussbaum AG 90024.43 de Visibility=Nein; R. Nussbaum AG 90024.44 de Visibility=Nein; R. Nussbaum AG 90024.45 de Visibility=Nein; R. Nussbaum AG 90024.46 de Visibility=Nein; Typenkommentare=Optifitt-Serra-Réduction DN=25x20; URL=https://www.nussbaum.ch
- DN=25x15: 1.800.00.3 TGA-Nummer=01900300000000000000000000000000000000000000000014000000000000000007; 1.800.00.4 Kommentarfeld=90024.28, Optifitt-Serra-Reduktion, DN=25x15, L=28, R=1, Rp=½; 1.810.00.3 Hersteller-Bestellnummer=90024.28; 1.810.00.4 DATANORM-Nummer=90024.28; 1.810.00.6 GTIN-Nummer=7612945033475; 29.710.02.10 Formstück-Gewicht [kg]=0.091; 29.710.02.3 Benennung=Optifitt-Serra-Reduktion, DN=25x15, L=28, R=1, Rp=½; CONNECTOR0_DIAMETER_dX_0r=15 mm; CONNECTOR0_dX_01=13 mm; CONNECTOR0_ref_dX=13 mm; CONNECTOR1_DIAMETER_dX_0r=25 mm  [stored 0.082021 ft]; CONNECTOR1_dX_00=11 mm; CONNECTOR1_dX_01=28 mm; CONNECTOR1_ref_dX=28 mm; R. Nussbaum AG 90024.20 de Visibility=Nein; R. Nussbaum AG 90024.21 de Visibility=Nein; R. Nussbaum AG 90024.22 de Visibility=Nein; R. Nussbaum AG 90024.23 de Visibility=Nein; R. Nussbaum AG 90024.25 de Visibility=Nein; R. Nussbaum AG 90024.26 de Visibility=Nein; R. Nussbaum AG 90024.27 de Visibility=Nein; R. Nussbaum AG 90024.28 de Visibility=Ja; R. Nussbaum AG 90024.29 de Visibility=Nein; R. Nussbaum AG 90024.30 de Visibility=Nein; R. Nussbaum AG 90024.31 de Visibility=Nein; R. Nussbaum AG 90024.32 de Visibility=Nein; R. Nussbaum AG 90024.33 de Visibility=Nein; R. Nussbaum AG 90024.34 de Visibility=Nein; R. Nussbaum AG 90024.35 de Visibility=Nein; R. Nussbaum AG 90024.36 de Visibility=Nein; R. Nussbaum AG 90024.37 de Visibility=Nein; R. Nussbaum AG 90024.38 de Visibility=Nein; R. Nussbaum AG 90024.39 de Visibility=Nein; R. Nussbaum AG 90024.40 de Visibility=Nein; R. Nussbaum AG 90024.41 de Visibility=Nein; R. Nussbaum AG 90024.42 de Visibility=Nein; R. Nussbaum AG 90024.43 de Visibility=Nein; R. Nussbaum AG 90024.44 de Visibility=Nein; R. Nussbaum AG 90024.45 de Visibility=Nein; R. Nussbaum AG 90024.46 de Visibility=Nein
- DN=25x12: 1.800.00.3 TGA-Nummer=01900300000000000000000000000000000000000000000014000000000000000006; 1.800.00.4 Kommentarfeld=90024.27, Optifitt-Serra-Reduktion, DN=25x12, L=27, R=1, Rp=3/8; 1.810.00.3 Hersteller-Bestellnummer=90024.27; 1.810.00.4 DATANORM-Nummer=90024.27; 1.810.00.6 GTIN-Nummer=7612945033468; 29.710.02.10 Formstück-Gewicht [kg]=0.098; 29.710.02.3 Benennung=Optifitt-Serra-Reduktion, DN=25x12, L=27, R=1, Rp=3/8; CONNECTOR0_DIAMETER_dX_0r=10 mm  [stored 0.0328084 ft]; CONNECTOR0_dX_01=10 mm  [stored 0.0328084 ft]; CONNECTOR0_ref_dX=10 mm  [stored 0.0328084 ft]; CONNECTOR1_DIAMETER_dX_0r=25 mm  [stored 0.082021 ft]; CONNECTOR1_dX_00=10 mm  [stored 0.0328084 ft]; CONNECTOR1_dX_01=27 mm; CONNECTOR1_ref_dX=27 mm; R. Nussbaum AG 90024.20 de Visibility=Nein; R. Nussbaum AG 90024.21 de Visibility=Nein; R. Nussbaum AG 90024.22 de Visibility=Nein; R. Nussbaum AG 90024.23 de Visibility=Nein; R. Nussbaum AG 90024.25 de Visibility=Nein; R. Nussbaum AG 90024.26 de Visibility=Nein; R. Nussbaum AG 90024.27 de Visibility=Ja; R. Nussbaum AG 90024.28 de Visibility=Nein; R. Nussbaum AG 90024.29 de Visibility=Nein; R. Nussbaum AG 90024.30 de Visibility=Nein; R. Nussbaum AG 90024.31 de Visibility=Nein; R. Nussbaum AG 90024.32 de Visibility=Nein; R. Nussbaum AG 90024.33 de Visibility=Nein; R. Nussbaum AG 90024.34 de Visibility=Nein; R. Nussbaum AG 90024.35 de Visibility=Nein; R. Nussbaum AG 90024.36 de Visibility=Nein; R. Nussbaum AG 90024.37 de Visibility=Nein; R. Nussbaum AG 90024.38 de Visibility=Nein; R. Nussbaum AG 90024.39 de Visibility=Nein; R. Nussbaum AG 90024.40 de Visibility=Nein; R. Nussbaum AG 90024.41 de Visibility=Nein; R. Nussbaum AG 90024.42 de Visibility=Nein; R. Nussbaum AG 90024.43 de Visibility=Nein; R. Nussbaum AG 90024.44 de Visibility=Nein; R. Nussbaum AG 90024.45 de Visibility=Nein; R. Nussbaum AG 90024.46 de Visibility=Nein
- DN=20x15: 1.800.00.3 TGA-Nummer=01900300000000000000000000000000000000000000000014000000000000000005; 1.800.00.4 Kommentarfeld=90024.26, Optifitt-Serra-Reduktion, DN=20x15, L=24, R=¾, Rp=½; 1.810.00.3 Hersteller-Bestellnummer=90024.26; 1.810.00.4 DATANORM-Nummer=90024.26; 1.810.00.5 StLB-Nummer=214.533; 1.810.00.6 GTIN-Nummer=7612945033451; 29.710.02.10 Formstück-Gewicht [kg]=0.041; 29.710.02.3 Benennung=Optifitt-Serra-Reduktion, DN=20x15, L=24, R=¾, Rp=½; CONNECTOR0_DIAMETER_dX_0r=15 mm; CONNECTOR0_dX_01=13 mm; CONNECTOR0_ref_dX=13 mm; CONNECTOR1_DIAMETER_dX_0r=20 mm; CONNECTOR1_dX_00=8 mm  [stored 0.0262467 ft]; CONNECTOR1_dX_01=23 mm; CONNECTOR1_ref_dX=23 mm; R. Nussbaum AG 90024.20 de Visibility=Nein; R. Nussbaum AG 90024.21 de Visibility=Nein; R. Nussbaum AG 90024.22 de Visibility=Nein; R. Nussbaum AG 90024.23 de Visibility=Nein; R. Nussbaum AG 90024.25 de Visibility=Nein; R. Nussbaum AG 90024.26 de Visibility=Ja; R. Nussbaum AG 90024.27 de Visibility=Nein; R. Nussbaum AG 90024.28 de Visibility=Nein; R. Nussbaum AG 90024.29 de Visibility=Nein; R. Nussbaum AG 90024.30 de Visibility=Nein; R. Nussbaum AG 90024.31 de Visibility=Nein; R. Nussbaum AG 90024.32 de Visibility=Nein; R. Nussbaum AG 90024.33 de Visibility=Nein; R. Nussbaum AG 90024.34 de Visibility=Nein; R. Nussbaum AG 90024.35 de Visibility=Nein; R. Nussbaum AG 90024.36 de Visibility=Nein; R. Nussbaum AG 90024.37 de Visibility=Nein; R. Nussbaum AG 90024.38 de Visibility=Nein; R. Nussbaum AG 90024.39 de Visibility=Nein; R. Nussbaum AG 90024.40 de Visibility=Nein; R. Nussbaum AG 90024.41 de Visibility=Nein; R. Nussbaum AG 90024.42 de Visibility=Nein; R. Nussbaum AG 90024.43 de Visibility=Nein; R. Nussbaum AG 90024.44 de Visibility=Nein; R. Nussbaum AG 90024.45 de Visibility=Nein; R. Nussbaum AG 90024.46 de Visibility=Nein
- DN=20x12: 1.800.00.3 TGA-Nummer=01900300000000000000000000000000000000000000000014000000000000000004; 1.800.00.4 Kommentarfeld=90024.25, Optifitt-Serra-Reduktion, DN=20x12, L=23, R=¾, Rp=3/8; 1.810.00.3 Hersteller-Bestellnummer=90024.25; 1.810.00.4 DATANORM-Nummer=90024.25; 1.810.00.6 GTIN-Nummer=7612945033444; 29.710.02.10 Formstück-Gewicht [kg]=0.049; 29.710.02.3 Benennung=Optifitt-Serra-Reduktion, DN=20x12, L=23, R=¾, Rp=3/8; CONNECTOR0_DIAMETER_dX_0r=10 mm  [stored 0.0328084 ft]; CONNECTOR0_dX_01=10 mm  [stored 0.0328084 ft]; CONNECTOR0_ref_dX=10 mm  [stored 0.0328084 ft]; CONNECTOR1_DIAMETER_dX_0r=20 mm; CONNECTOR1_dX_00=8 mm  [stored 0.0262467 ft]; CONNECTOR1_dX_01=23 mm; CONNECTOR1_ref_dX=23 mm; R. Nussbaum AG 90024.20 de Visibility=Nein; R. Nussbaum AG 90024.21 de Visibility=Nein; R. Nussbaum AG 90024.22 de Visibility=Nein; R. Nussbaum AG 90024.23 de Visibility=Nein; R. Nussbaum AG 90024.25 de Visibility=Ja; R. Nussbaum AG 90024.26 de Visibility=Nein; R. Nussbaum AG 90024.27 de Visibility=Nein; R. Nussbaum AG 90024.28 de Visibility=Nein; R. Nussbaum AG 90024.29 de Visibility=Nein; R. Nussbaum AG 90024.30 de Visibility=Nein; R. Nussbaum AG 90024.31 de Visibility=Nein; R. Nussbaum AG 90024.32 de Visibility=Nein; R. Nussbaum AG 90024.33 de Visibility=Nein; R. Nussbaum AG 90024.34 de Visibility=Nein; R. Nussbaum AG 90024.35 de Visibility=Nein; R. Nussbaum AG 90024.36 de Visibility=Nein; R. Nussbaum AG 90024.37 de Visibility=Nein; R. Nussbaum AG 90024.38 de Visibility=Nein; R. Nussbaum AG 90024.39 de Visibility=Nein; R. Nussbaum AG 90024.40 de Visibility=Nein; R. Nussbaum AG 90024.41 de Visibility=Nein; R. Nussbaum AG 90024.42 de Visibility=Nein; R. Nussbaum AG 90024.43 de Visibility=Nein; R. Nussbaum AG 90024.44 de Visibility=Nein; R. Nussbaum AG 90024.45 de Visibility=Nein; R. Nussbaum AG 90024.46 de Visibility=Nein
- DN=15x12: 1.800.00.3 TGA-Nummer=01900300000000000000000000000000000000000000000014000000000000000003; 1.800.00.4 Kommentarfeld=90024.23, Optifitt-Serra-Reduktion, DN=15x12, L=22, R=½, Rp=3/8; 1.810.00.3 Hersteller-Bestellnummer=90024.23; 1.810.00.4 DATANORM-Nummer=90024.23; 1.810.00.5 StLB-Nummer=214.532; 1.810.00.6 GTIN-Nummer=7612945033437; 29.710.02.10 Formstück-Gewicht [kg]=0.024; 29.710.02.3 Benennung=Optifitt-Serra-Reduktion, DN=15x12, L=22, R=½, Rp=3/8; CONNECTOR0_DIAMETER_dX_0r=10 mm  [stored 0.0328084 ft]; CONNECTOR0_dX_01=10 mm  [stored 0.0328084 ft]; CONNECTOR0_ref_dX=10 mm  [stored 0.0328084 ft]; CONNECTOR1_DIAMETER_dX_0r=15 mm; CONNECTOR1_dX_00=9 mm  [stored 0.0295276 ft]; CONNECTOR1_dX_01=22 mm; CONNECTOR1_ref_dX=22 mm; R. Nussbaum AG 90024.20 de Visibility=Nein; R. Nussbaum AG 90024.21 de Visibility=Nein; R. Nussbaum AG 90024.22 de Visibility=Nein; R. Nussbaum AG 90024.23 de Visibility=Ja; R. Nussbaum AG 90024.25 de Visibility=Nein; R. Nussbaum AG 90024.26 de Visibility=Nein; R. Nussbaum AG 90024.27 de Visibility=Nein; R. Nussbaum AG 90024.28 de Visibility=Nein; R. Nussbaum AG 90024.29 de Visibility=Nein; R. Nussbaum AG 90024.30 de Visibility=Nein; R. Nussbaum AG 90024.31 de Visibility=Nein; R. Nussbaum AG 90024.32 de Visibility=Nein; R. Nussbaum AG 90024.33 de Visibility=Nein; R. Nussbaum AG 90024.34 de Visibility=Nein; R. Nussbaum AG 90024.35 de Visibility=Nein; R. Nussbaum AG 90024.36 de Visibility=Nein; R. Nussbaum AG 90024.37 de Visibility=Nein; R. Nussbaum AG 90024.38 de Visibility=Nein; R. Nussbaum AG 90024.39 de Visibility=Nein; R. Nussbaum AG 90024.40 de Visibility=Nein; R. Nussbaum AG 90024.41 de Visibility=Nein; R. Nussbaum AG 90024.42 de Visibility=Nein; R. Nussbaum AG 90024.43 de Visibility=Nein; R. Nussbaum AG 90024.44 de Visibility=Nein; R. Nussbaum AG 90024.45 de Visibility=Nein; R. Nussbaum AG 90024.46 de Visibility=Nein
- DN=15x6: 1.800.00.3 TGA-Nummer=01900300000000000000000000000000000000000000000014000000000000000002; 1.800.00.4 Kommentarfeld=90024.22, Optifitt-Serra-Reduktion, DN=15x6, L=22, R=½, Rp=¼; 1.810.00.3 Hersteller-Bestellnummer=90024.22; 1.810.00.4 DATANORM-Nummer=90024.22; 1.810.00.6 GTIN-Nummer=7612945033420; 29.710.02.10 Formstück-Gewicht [kg]=0.032; 29.710.02.3 Benennung=Optifitt-Serra-Reduktion, DN=15x6, L=22, R=½, Rp=¼; CONNECTOR0_DIAMETER_dX_0r=8 mm  [stored 0.0262467 ft]; CONNECTOR0_dX_01=10 mm  [stored 0.0328084 ft]; CONNECTOR0_ref_dX=10 mm  [stored 0.0328084 ft]; CONNECTOR1_DIAMETER_dX_0r=15 mm; CONNECTOR1_dX_00=9 mm  [stored 0.0295276 ft]; CONNECTOR1_dX_01=22 mm; CONNECTOR1_ref_dX=22 mm; R. Nussbaum AG 90024.20 de Visibility=Nein; R. Nussbaum AG 90024.21 de Visibility=Nein; R. Nussbaum AG 90024.22 de Visibility=Ja; R. Nussbaum AG 90024.23 de Visibility=Nein; R. Nussbaum AG 90024.25 de Visibility=Nein; R. Nussbaum AG 90024.26 de Visibility=Nein; R. Nussbaum AG 90024.27 de Visibility=Nein; R. Nussbaum AG 90024.28 de Visibility=Nein; R. Nussbaum AG 90024.29 de Visibility=Nein; R. Nussbaum AG 90024.30 de Visibility=Nein; R. Nussbaum AG 90024.31 de Visibility=Nein; R. Nussbaum AG 90024.32 de Visibility=Nein; R. Nussbaum AG 90024.33 de Visibility=Nein; R. Nussbaum AG 90024.34 de Visibility=Nein; R. Nussbaum AG 90024.35 de Visibility=Nein; R. Nussbaum AG 90024.36 de Visibility=Nein; R. Nussbaum AG 90024.37 de Visibility=Nein; R. Nussbaum AG 90024.38 de Visibility=Nein; R. Nussbaum AG 90024.39 de Visibility=Nein; R. Nussbaum AG 90024.40 de Visibility=Nein; R. Nussbaum AG 90024.41 de Visibility=Nein; R. Nussbaum AG 90024.42 de Visibility=Nein; R. Nussbaum AG 90024.43 de Visibility=Nein; R. Nussbaum AG 90024.44 de Visibility=Nein; R. Nussbaum AG 90024.45 de Visibility=Nein; R. Nussbaum AG 90024.46 de Visibility=Nein
- DN=12x10: 1.800.00.3 TGA-Nummer=01900300000000000000000000000000000000000000000014000000000000000001; 1.800.00.4 Kommentarfeld=90024.21, Optifitt-Serra-Reduktion, DN=12x10, L=17, R=3/8, Rp=¼; 1.810.00.3 Hersteller-Bestellnummer=90024.21; 1.810.00.4 DATANORM-Nummer=90024.21; 1.810.00.5 StLB-Nummer=214.531; 1.810.00.6 GTIN-Nummer=7612945033413; 29.710.02.10 Formstück-Gewicht [kg]=0.013; 29.710.02.3 Benennung=Optifitt-Serra-Reduktion, DN=12x10, L=17, R=3/8, Rp=¼; CONNECTOR0_DIAMETER_dX_0r=8 mm  [stored 0.0262467 ft]; CONNECTOR0_dX_01=10 mm  [stored 0.0328084 ft]; CONNECTOR0_ref_dX=10 mm  [stored 0.0328084 ft]; CONNECTOR1_DIAMETER_dX_0r=10 mm  [stored 0.0328084 ft]; CONNECTOR1_dX_00=7 mm  [stored 0.0229659 ft]; CONNECTOR1_dX_01=17 mm; CONNECTOR1_ref_dX=17 mm; R. Nussbaum AG 90024.20 de Visibility=Nein; R. Nussbaum AG 90024.21 de Visibility=Ja; R. Nussbaum AG 90024.22 de Visibility=Nein; R. Nussbaum AG 90024.23 de Visibility=Nein; R. Nussbaum AG 90024.25 de Visibility=Nein; R. Nussbaum AG 90024.26 de Visibility=Nein; R. Nussbaum AG 90024.27 de Visibility=Nein; R. Nussbaum AG 90024.28 de Visibility=Nein; R. Nussbaum AG 90024.29 de Visibility=Nein; R. Nussbaum AG 90024.30 de Visibility=Nein; R. Nussbaum AG 90024.31 de Visibility=Nein; R. Nussbaum AG 90024.32 de Visibility=Nein; R. Nussbaum AG 90024.33 de Visibility=Nein; R. Nussbaum AG 90024.34 de Visibility=Nein; R. Nussbaum AG 90024.35 de Visibility=Nein; R. Nussbaum AG 90024.36 de Visibility=Nein; R. Nussbaum AG 90024.37 de Visibility=Nein; R. Nussbaum AG 90024.38 de Visibility=Nein; R. Nussbaum AG 90024.39 de Visibility=Nein; R. Nussbaum AG 90024.40 de Visibility=Nein; R. Nussbaum AG 90024.41 de Visibility=Nein; R. Nussbaum AG 90024.42 de Visibility=Nein; R. Nussbaum AG 90024.43 de Visibility=Nein; R. Nussbaum AG 90024.44 de Visibility=Nein; R. Nussbaum AG 90024.45 de Visibility=Nein; R. Nussbaum AG 90024.46 de Visibility=Nein

note: [stored X ft] marks values corroborated as IEEE doubles in the binary element streams (Revit-internal decimal feet)

## geometry (parser evidence)
native form markers: Sweep x3
no freeform markers — native parametric forms only
